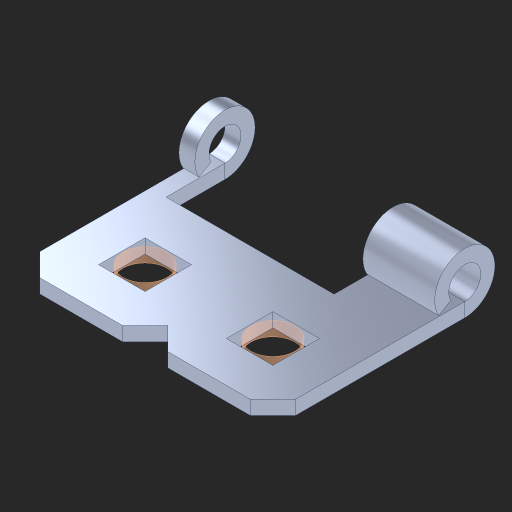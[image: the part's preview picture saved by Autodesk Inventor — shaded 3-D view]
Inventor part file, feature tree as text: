
AUTODESK INVENTOR PART (.ipt)
format: ipt  version: 2023 (Build 270158000, 158)  size: 201,728 bytes
history: native  units: in
note: dims shown in document units (in); Inventor stores cm internally (conversion verified against a paired STEP export)
features: other x4, extrude x3, sketch x2, pattern_linear x1, imported_body x1
ambient origin geometry x8: Origin, YZ Plane, XZ Plane, XY Plane, X Axis, Y Axis, Z Axis, Center Point
bodies: Body1 (feature_tree), Body2 (feature_tree), Body3 (feature_tree)
feature tree (11):
  other  "Cut-Extrude3"
  other  "Top"
  pattern_linear  "Rectangular Pattern2"  Spacing1=0.5in  [1 undecoded]
  extrude  "Extrusion1"  Depth=0.5in
  imported_body  "Base1"
  sketch  "Sketch4"  dims[d30=0.172in]
  other  "Srf6"
  other  "Srf7"
  sketch  "Sketch5"  dims[d31=0.055in d32=0.0in d35=0.5in d36=1.5in d37=0.0in]
  extrude  "ExtrusionSrf6"  TaperAngle=0.0deg  [1 undecoded]
  extrude  "ExtrusionSrf7"  [1 undecoded]
note: 3 required parameter values undecoded (feature->parameter linkage not recoverable at this tier; creation-order binding heuristic only, values carry confidence <= 0.55)
